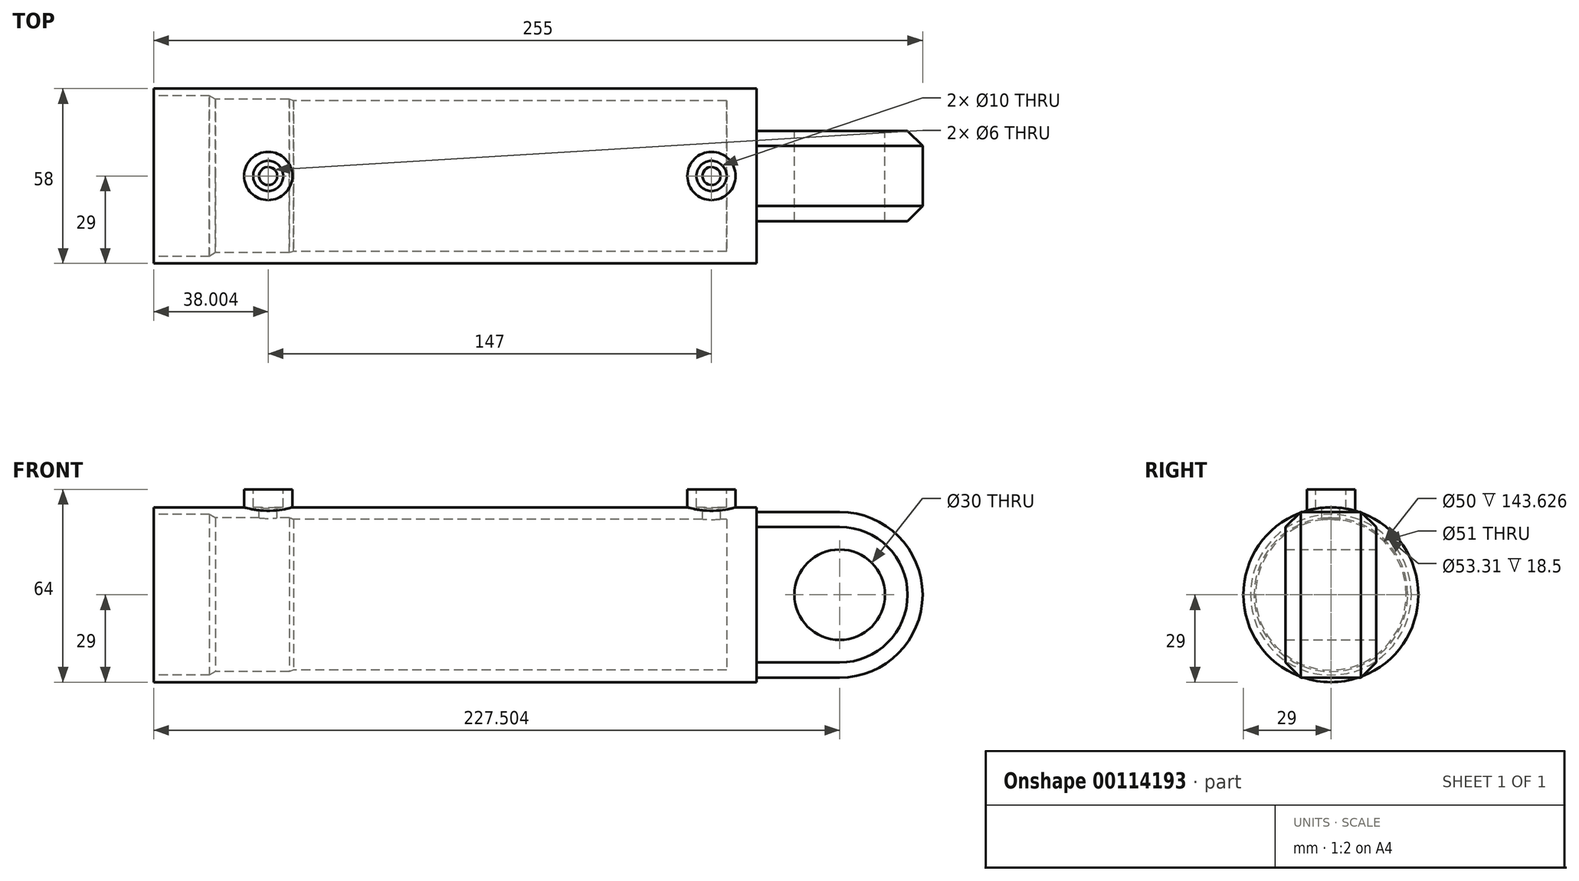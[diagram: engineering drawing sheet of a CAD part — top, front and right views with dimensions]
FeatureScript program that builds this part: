
annotation { "Feature Type Name" : "Feature", "Feature Type Description" : "" }
export const myFeature = defineFeature(function(context is Context, id is Id, definition is map)
    precondition{}
    {
        {
            var Q0;
            Q0=qCreatedBy(makeId("Front.planeOp"),FACE);
            var sketch = newSketch(context, id + "F0", { "sketchPlane" : qUnion([Q0])});
            skLineSegment(sketch, "E0", {"start": v(0, 0) * mm, "end": v(250.98, 0) * mm});
            skCircle(sketch, "E1", {"center": v(0, 0) * mm, "radius": 15 * mm});
            skCircle(sketch, "E2", {"center": v(0, 0) * mm, "radius": 27.5 * mm});
            skLineSegment(sketch, "E3", {"start": v(24.5, 12.5) * mm, "end": v(205, 12.5) * mm});
            skLineSegment(sketch, "E4", {"start": v(250, 8) * mm, "end": v(250, 0) * mm});
            skLineSegment(sketch, "E5", {"start": v(205, 12.5) * mm, "end": v(205, 8.5) * mm});
            skLineSegment(sketch, "E6", {"start": v(205, 8.5) * mm, "end": v(225, 8.5) * mm});
            skLineSegment(sketch, "E7", {"start": v(225, 8.5) * mm, "end": v(225, 8) * mm});
            skLineSegment(sketch, "E8", {"start": v(225, 8) * mm, "end": v(250, 8) * mm});
            skSolve(sketch);
        }
        {
            var Q0;
            Q0=qCreatedBy(makeId("Front.planeOp"),FACE);
            var sketch = newSketch(context, id + "F1", { "sketchPlane" : qUnion([Q0])});
            skLineSegment(sketch, "E9", {"start": v(54.7, 12.5) * mm, "end": v(54.7, 29) * mm});
            skLineSegment(sketch, "E10", {"start": v(54.7, 29) * mm, "end": v(60.7, 29) * mm});
            skLineSegment(sketch, "E11", {"start": v(60.7, 29) * mm, "end": v(60.7, 27.5) * mm});
            skLineSegment(sketch, "E12", {"start": v(60.7, 27.5) * mm, "end": v(76.24, 27.5) * mm});
            skLineSegment(sketch, "E13", {"start": v(76.24, 27.5) * mm, "end": v(79.7, 25.5) * mm});
            skLineSegment(sketch, "E14", {"start": v(79.7, 25.5) * mm, "end": v(94.7, 25.5) * mm});
            skLineSegment(sketch, "E15", {"start": v(94.7, 25.5) * mm, "end": v(94.7, 12.5) * mm});
            skLineSegment(sketch, "E16", {"start": v(94.7, 12.5) * mm, "end": v(54.7, 12.5) * mm});
            skLineSegment(sketch, "E17", {"start": v(66.7, 12.5) * mm, "end": v(66.7, 18) * mm});
            skLineSegment(sketch, "E18", {"start": v(66.7, 18) * mm, "end": v(76.7, 18) * mm});
            skLineSegment(sketch, "E19", {"start": v(76.7, 18) * mm, "end": v(76.7, 12.5) * mm});
            skLineSegment(sketch, "E20", {"start": v(54.7, 14) * mm, "end": v(56.7, 14) * mm});
            skLineSegment(sketch, "E21", {"start": v(56.7, 14) * mm, "end": v(56.7, 16) * mm});
            skLineSegment(sketch, "E22", {"start": v(56.7, 16) * mm, "end": v(60.7, 16) * mm});
            skLineSegment(sketch, "E23", {"start": v(60.7, 16) * mm, "end": v(60.7, 12.5) * mm});
            skLineSegment(sketch, "E24.bottom", {"start": v(85.7, 25.5) * mm, "end": v(89.7, 25.5) * mm});
            skLineSegment(sketch, "E24.top", {"start": v(85.7, 23.5) * mm, "end": v(89.7, 23.5) * mm});
            skLineSegment(sketch, "E24.left", {"start": v(85.7, 25.5) * mm, "end": v(85.7, 23.5) * mm});
            skLineSegment(sketch, "E24.right", {"start": v(89.7, 25.5) * mm, "end": v(89.7, 23.5) * mm});
            skLineSegment(sketch, "E25", {"start": v(48.25, 0) * mm, "end": v(103.65, 0) * mm});
            skSolve(sketch);
        }
        {
            var Q0;
            Q0=qCreatedBy(makeId("Front.planeOp"),FACE);
            var sketch = newSketch(context, id + "F2", { "sketchPlane" : qUnion([Q0])});
            skLineSegment(sketch, "E26.bottom", {"start": v(60.7, 29) * mm, "end": v(260.7, 29) * mm});
            skLineSegment(sketch, "E26.top", {"start": v(107.08, 25) * mm, "end": v(250.7, 25) * mm});
            skLineSegment(sketch, "E26.left", {"start": v(60.7, 29) * mm, "end": v(60.7, 26.65) * mm});
            skLineSegment(sketch, "E27", {"start": v(250.7, 25) * mm, "end": v(250.7, 0) * mm});
            skLineSegment(sketch, "E28", {"start": v(250.7, 0) * mm, "end": v(288.2, 0) * mm});
            skCircle(sketch, "E29", {"center": v(288.2, 0) * mm, "radius": 15 * mm});
            skArc(sketch, "E30", {"start": v(288.2, -27.5) * mm, "mid": v(315.7, 0) * mm, "end": v(288.2, 27.5) * mm});
            skLineSegment(sketch, "E31", {"start": v(260.7, 0) * mm, "end": v(260.7, 29) * mm});
            skLineSegment(sketch, "E32", {"start": v(288.2, 27.5) * mm, "end": v(260.7, 27.5) * mm});
            skLineSegment(sketch, "E33", {"start": v(288.2, -27.5) * mm, "end": v(260.7, -27.5) * mm});
            skLineSegment(sketch, "E34", {"start": v(260.7, -27.5) * mm, "end": v(260.7, 0) * mm});
            skLineSegment(sketch, "E35", {"start": v(107.08, 25) * mm, "end": v(105.7, 25.5) * mm});
            skLineSegment(sketch, "E36", {"start": v(105.7, 25.5) * mm, "end": v(81.2, 25.5) * mm});
            skLineSegment(sketch, "E37", {"start": v(81.2, 25.5) * mm, "end": v(79.2, 26.65) * mm});
            skLineSegment(sketch, "E38", {"start": v(79.2, 26.65) * mm, "end": v(60.7, 26.65) * mm});
            skLineSegment(sketch, "E39", {"start": v(92.36, 29) * mm, "end": v(92.36, 40.1) * mm});
            skLineSegment(sketch, "E40", {"start": v(92.36, 40.1) * mm, "end": v(105.05, 40.1) * mm});
            skLineSegment(sketch, "E41", {"start": v(105.05, 40.1) * mm, "end": v(105.05, 29) * mm});
            skLineSegment(sketch, "E42", {"start": v(98.7, 40.1) * mm, "end": v(98.7, 23.63) * mm});
            skSolve(sketch);
        }
        {
            var Q0;
            Q0=makeQuery(id+"F2.imprint","IMPRINT",FACE,{"disambiguationData":[TD([[makeQuery(id+"F2.imprint","IMPRINT",EDGE,{"derivedFrom":sQuery(id+"F2.wireOp",EDGE,"E26.top")}),1.0]])]});
            var Q1;
            {var subQ4=sQuery(id+"F2.wireOp",EDGE,"E26.left");Q1=makeQuery(id+"F2.imprint","IMPRINT",FACE,{"disambiguationData":[TD([[makeQuery(id+"F2.imprint","IMPRINT",EDGE,{"derivedFrom":subQ4}),1.0]])]});}
            var Q2;
            Q2=sQuery(id+"F0.wireOp",EDGE,"E0");
            revolve(context, id + "F3", {"entities" : qUnion([Q0, Q1]), "axis" : qUnion([Q2]), "revolveType" : RevolveType.FULL});
        }
        {
            var Q0;
            Q0=makeQuery(id+"F2.imprint","IMPRINT",FACE,{"disambiguationData":[TD([[makeQuery(id+"F2.imprint","IMPRINT",EDGE,{"derivedFrom":sQuery(id+"F2.wireOp",EDGE,"E29")}),-1.0]])]});
            extrude(context, id + "F4", {"entities" : qUnion([Q0]), "operationType" : NewBodyOperationType.ADD, "endBound" : BoundingType.SYMMETRIC, "depth" : 30 * mm});
        }
        {
            var Q0;
            Q0=makeQuery(id+"F4.opExtrude","CAP_EDGE",EDGE,{"disambiguationData":[OSD([sQuery(id+"F2.wireOp",EDGE,"E32")])],"isStart":false});
            var Q1;
            Q1=makeQuery(id+"F4.opExtrude","CAP_EDGE",EDGE,{"disambiguationData":[OSD([sQuery(id+"F2.wireOp",EDGE,"E30")])],"isStart":true});
            chamfer(context, id + "F5", {"entities" : qUnion([Q0, Q1]), "width" : 5 * mm, "tangentPropagation" : true});
        }
        {
            var Q0;
            Q0=qCreatedBy(makeId("Top.planeOp"),FACE);
            cPlane(context, id + "F6", {"entities" : qUnion([Q0]), "cplaneType" : CPlaneType.OFFSET, "offset" : 35 * mm, "width" : 150 * mm, "height" : 150 * mm});
        }
        {
            var Q0;
            Q0=qCreatedBy(id+"F6.planeOp",FACE);
            var sketch = newSketch(context, id + "F7", { "sketchPlane" : qUnion([Q0])});
            skCircle(sketch, "E43", {"center": v(98.7, 0) * mm, "radius": 8 * mm});
            skCircle(sketch, "E44", {"center": v(98.7, 0) * mm, "radius": 5 * mm});
            skCircle(sketch, "E45", {"center": v(245.7, 0) * mm, "radius": 8 * mm});
            skCircle(sketch, "E46", {"center": v(245.7, 0) * mm, "radius": 5 * mm});
            skSolve(sketch);
        }
        {
            var Q0;
            Q0=makeQuery(id+"F7.imprint","IMPRINT",FACE,{"disambiguationData":[TD([[makeQuery(id+"F7.imprint","IMPRINT",EDGE,{"derivedFrom":sQuery(id+"F7.wireOp",EDGE,"E43")}),1.0]])]});
            var Q1;
            Q1=makeQuery(id+"F7.imprint","IMPRINT",FACE,{"disambiguationData":[TD([[makeQuery(id+"F7.imprint","IMPRINT",EDGE,{"derivedFrom":sQuery(id+"F7.wireOp",EDGE,"E45")}),1.0]])]});
            var Q2;
            Q2=makeQuery(id+"F3.opRevolve","SWEPT_FACE",FACE,{"disambiguationData":[OSD([sQuery(id+"F2.wireOp",EDGE,"E26.bottom")])]});
            extrude(context, id + "F8", {"entities" : qUnion([Q0, Q1]), "operationType" : NewBodyOperationType.ADD, "endBound" : BoundingType.UP_TO_SURFACE, "oppositeDirection" : true, "endBoundEntityFace" : qUnion([Q2]), "depth" : 25 * mm});
        }
        {
            var Q0;
            Q0=sQuery(id+"F7.wireOp",VERTEX,"E44.center");
            var Q1;
            Q1=makeQuery(id+"F3.opRevolve","SWEPT_BODY",BODY,{"disambiguationData":[OSD([sQuery(id+"F2.wireOp",EDGE,"E26.bottom"),sQuery(id+"F2.wireOp",EDGE,"E26.top"),sQuery(id+"F2.wireOp",EDGE,"E26.left"),sQuery(id+"F2.wireOp",EDGE,"E27"),sQuery(id+"F2.wireOp",EDGE,"E28"),sQuery(id+"F2.wireOp",EDGE,"E31"),sQuery(id+"F2.wireOp",EDGE,"E35"),sQuery(id+"F2.wireOp",EDGE,"E36"),sQuery(id+"F2.wireOp",EDGE,"E37"),sQuery(id+"F2.wireOp",EDGE,"E38")])]});
            hole(context, id + "F9", {"style" : HoleStyle.SIMPLE, "endStyle" : HoleEndStyle.BLIND, "holeDiameter" : 6 * mm, "holeDepth" : 20 * mm, "locations" : qUnion([Q0]), "scope" : qUnion([Q1])});
        }
        {
            var Q0;
            Q0=sQuery(id+"F7.wireOp",VERTEX,"E45.center");
            var Q1;
            Q1=makeQuery(id+"F3.opRevolve","SWEPT_BODY",BODY,{"disambiguationData":[OSD([sQuery(id+"F2.wireOp",EDGE,"E26.bottom"),sQuery(id+"F2.wireOp",EDGE,"E26.top"),sQuery(id+"F2.wireOp",EDGE,"E26.left"),sQuery(id+"F2.wireOp",EDGE,"E27"),sQuery(id+"F2.wireOp",EDGE,"E28"),sQuery(id+"F2.wireOp",EDGE,"E31"),sQuery(id+"F2.wireOp",EDGE,"E35"),sQuery(id+"F2.wireOp",EDGE,"E36"),sQuery(id+"F2.wireOp",EDGE,"E37"),sQuery(id+"F2.wireOp",EDGE,"E38")])]});
            hole(context, id + "F10", {"style" : HoleStyle.SIMPLE, "endStyle" : HoleEndStyle.BLIND, "holeDiameter" : 6 * mm, "holeDepth" : 20 * mm, "locations" : qUnion([Q0]), "scope" : qUnion([Q1])});
        }
    });
